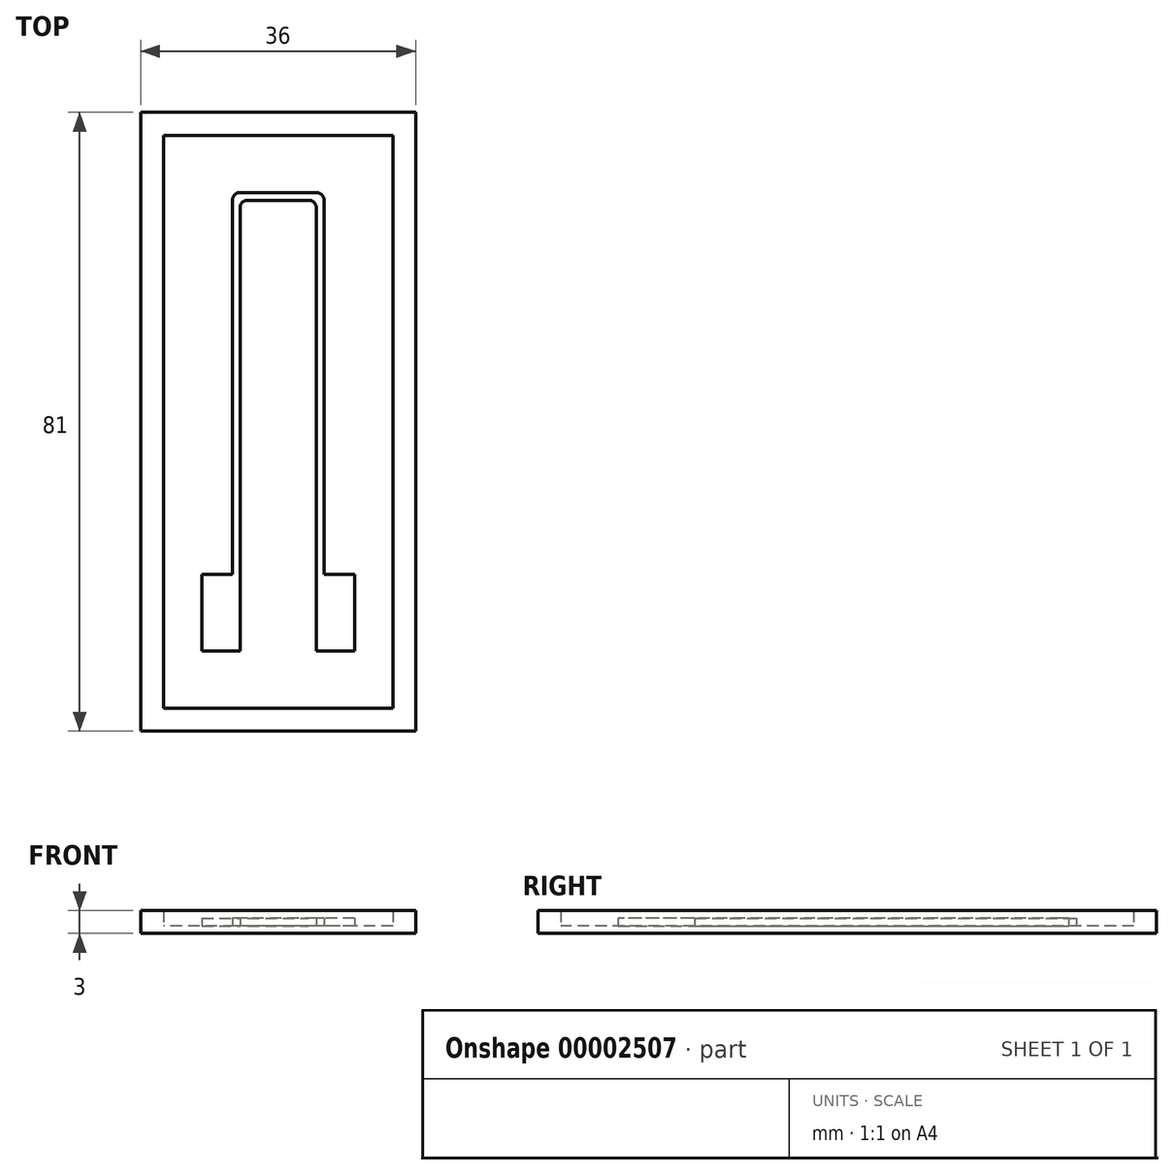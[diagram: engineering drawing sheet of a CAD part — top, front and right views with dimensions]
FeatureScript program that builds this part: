
annotation { "Feature Type Name" : "Feature", "Feature Type Description" : "" }
export const myFeature = defineFeature(function(context is Context, id is Id, definition is map)
    precondition{}
    {
        {
            var Q0;
            Q0=qCreatedBy(makeId("Top.planeOp"),FACE);
            var sketch = newSketch(context, id + "F0", { "sketchPlane" : qUnion([Q0])});
            skLineSegment(sketch, "E0.rect.bottom", {"start": v(15, 37.5) * mm, "end": v(-15, 37.5) * mm});
            skLineSegment(sketch, "E0.rect.top", {"start": v(15, -37.5) * mm, "end": v(-15, -37.5) * mm});
            skLineSegment(sketch, "E0.rect.left", {"start": v(15, 37.5) * mm, "end": v(15, -37.5) * mm});
            skLineSegment(sketch, "E0.rect.right", {"start": v(-15, 37.5) * mm, "end": v(-15, -37.5) * mm});
            skPoint(sketch, "E0.rect.middle", {"position": v(0, 0) * mm});
            skLineSegment(sketch, "E1", {"start": v(0, 0) * mm, "end": v(0, 17.9) * mm, "construction": true});
            skLineSegment(sketch, "E2.bottom", {"start": v(-10, -20) * mm, "end": v(-6, -20) * mm});
            skLineSegment(sketch, "E2.top", {"start": v(-10, -30) * mm, "end": v(-5, -30) * mm});
            skLineSegment(sketch, "E2.left", {"start": v(-10, -20) * mm, "end": v(-10, -30) * mm});
            skLineSegment(sketch, "E2.right", {"start": v(-5, -20) * mm, "end": v(-5, -30) * mm});
            skLineSegment(sketch, "E3", {"start": v(-5, -20) * mm, "end": v(-5, 28) * mm});
            skLineSegment(sketch, "E4", {"start": v(-4, 29) * mm, "end": v(0, 29) * mm});
            skLineSegment(sketch, "E5", {"start": v(-6, -20) * mm, "end": v(-6, 29) * mm});
            skLineSegment(sketch, "E6", {"start": v(-5, 30) * mm, "end": v(0, 30) * mm});
            skPoint(sketch, "E7.visualSharp", {"position": v(-6, 30) * mm});
            skArc(sketch, "E7.filletArc", {"start": v(-5, 30) * mm, "mid": v(-5.7, 29.7) * mm, "end": v(-6, 29) * mm});
            skArc(sketch, "E8.filletArc", {"start": v(-4, 29) * mm, "mid": v(-4.7, 28.7) * mm, "end": v(-5, 28) * mm});
            skLineSegment(sketch, "E9.0.MirrorCS", {"start": v(10, -30) * mm, "end": v(5, -30) * mm});
            skArc(sketch, "E9.1.MirrorCS", {"start": v(4, 29) * mm, "mid": v(4.7, 28.7) * mm, "end": v(5, 28) * mm});
            skArc(sketch, "E9.2.MirrorCS", {"start": v(5, 30) * mm, "mid": v(5.7, 29.7) * mm, "end": v(6, 29) * mm});
            skLineSegment(sketch, "E9.3.MirrorCS", {"start": v(10, -20) * mm, "end": v(6, -20) * mm});
            skLineSegment(sketch, "E9.4.MirrorCS", {"start": v(4, 29) * mm, "end": v(0, 29) * mm});
            skLineSegment(sketch, "E9.5.MirrorCS", {"start": v(5, 30) * mm, "end": v(0, 30) * mm});
            skPoint(sketch, "E9.6.MirrorP", {"position": v(6, 30) * mm});
            skLineSegment(sketch, "E9.8.MirrorCS", {"start": v(5, -20) * mm, "end": v(5, -30) * mm});
            skPoint(sketch, "E9.9.MirrorP", {"position": v(5, 29) * mm});
            skLineSegment(sketch, "E9.10.MirrorCS", {"start": v(6, -20) * mm, "end": v(6, 29) * mm});
            skLineSegment(sketch, "E9.11.MirrorCS", {"start": v(10, -20) * mm, "end": v(10, -30) * mm});
            skLineSegment(sketch, "E9.12.MirrorCS", {"start": v(5, -20) * mm, "end": v(5, 28) * mm});
            skLineSegment(sketch, "E10.0", {"start": v(18, 40.5) * mm, "end": v(-18, 40.5) * mm});
            skLineSegment(sketch, "E10.1", {"start": v(18, 40.5) * mm, "end": v(18, -40.5) * mm});
            skLineSegment(sketch, "E10.2", {"start": v(18, -40.5) * mm, "end": v(-18, -40.5) * mm});
            skLineSegment(sketch, "E10.3", {"start": v(-18, 40.5) * mm, "end": v(-18, -40.5) * mm});
            skSolve(sketch);
        }
        {
            var Q0;
            Q0=makeQuery(id+"F0.imprint","IMPRINT",FACE,{"disambiguationData":[TD([[makeQuery(id+"F0.imprint","IMPRINT",EDGE,{"derivedFrom":sQuery(id+"F0.wireOp",EDGE,"E0.rect.bottom")}),-1.0]])]});
            extrude(context, id + "F1", {"entities" : qUnion([Q0]), "depth" : 2 * mm});
        }
        {
            var Q0;
            Q0=makeQuery(id+"F0.imprint","IMPRINT",FACE,{"disambiguationData":[TD([[makeQuery(id+"F0.imprint","IMPRINT",EDGE,{"derivedFrom":sQuery(id+"F0.wireOp",EDGE,"E0.rect.bottom")}),1.0]])]});
            var Q1;
            Q1=makeQuery(id+"F1.opExtrude","CAP_FACE",FACE,{"disambiguationData":[OSD([sQuery(id+"F0.wireOp",EDGE,"E0.rect.bottom"),sQuery(id+"F0.wireOp",EDGE,"E0.rect.top"),sQuery(id+"F0.wireOp",EDGE,"E0.rect.left"),sQuery(id+"F0.wireOp",EDGE,"E0.rect.right"),sQuery(id+"F0.wireOp",EDGE,"E10.0"),sQuery(id+"F0.wireOp",EDGE,"E10.1"),sQuery(id+"F0.wireOp",EDGE,"E10.2"),sQuery(id+"F0.wireOp",EDGE,"E10.3")])],"isStart":false});
            var Q2;
            Q2=makeQuery(id+"F0.imprint","IMPRINT",FACE,{"disambiguationData":[TD([[makeQuery(id+"F0.imprint","IMPRINT",EDGE,{"derivedFrom":sQuery(id+"F0.wireOp",EDGE,"E2.bottom")}),-1.0]])]});
            extrude(context, id + "F2", {"entities" : qUnion([Q0, Q1, Q2]), "operationType" : NewBodyOperationType.ADD, "depth" : 1 * mm});
        }
        {
            var Q0;
            Q0=makeQuery(id+"F2.opExtrude","CAP_FACE",FACE,{"disambiguationData":[OSD([sQuery(id+"F0.wireOp",EDGE,"E0.rect.bottom"),sQuery(id+"F0.wireOp",EDGE,"E0.rect.top"),sQuery(id+"F0.wireOp",EDGE,"E0.rect.left"),sQuery(id+"F0.wireOp",EDGE,"E0.rect.right")])],"isStart":false});
            var sketch = newSketch(context, id + "F3", { "sketchPlane" : qUnion([Q0])});
            skLineSegment(sketch, "E11.0", {"start": v(-10, -20) * mm, "end": v(-10, -30) * mm});
            skLineSegment(sketch, "E12.0", {"start": v(-10, -30) * mm, "end": v(-5, -30) * mm});
            skLineSegment(sketch, "E13.0", {"start": v(-5, -20) * mm, "end": v(-5, -30) * mm});
            skLineSegment(sketch, "E14.0", {"start": v(-10, -20) * mm, "end": v(-6, -20) * mm});
            skLineSegment(sketch, "E15.0", {"start": v(-6, -20) * mm, "end": v(-6, 29) * mm});
            skLineSegment(sketch, "E16.0", {"start": v(-5, -20) * mm, "end": v(-5, 28) * mm});
            skArc(sketch, "E17.0", {"start": v(-5, 30) * mm, "mid": v(-5.7, 29.7) * mm, "end": v(-6, 29) * mm});
            skArc(sketch, "E18.0", {"start": v(-4, 29) * mm, "mid": v(-4.7, 28.7) * mm, "end": v(-5, 28) * mm});
            skLineSegment(sketch, "E19.0", {"start": v(-4, 29) * mm, "end": v(0, 29) * mm});
            skLineSegment(sketch, "E20.0", {"start": v(-5, 30) * mm, "end": v(0, 30) * mm});
            skLineSegment(sketch, "E21.0", {"start": v(4, 29) * mm, "end": v(0, 29) * mm});
            skLineSegment(sketch, "E22.0", {"start": v(5, 30) * mm, "end": v(0, 30) * mm});
            skArc(sketch, "E23.0", {"start": v(4, 29) * mm, "mid": v(4.7, 28.7) * mm, "end": v(5, 28) * mm});
            skArc(sketch, "E24.0", {"start": v(5, 30) * mm, "mid": v(5.7, 29.7) * mm, "end": v(6, 29) * mm});
            skLineSegment(sketch, "E25.0", {"start": v(5, -20) * mm, "end": v(5, 28) * mm});
            skLineSegment(sketch, "E26.0", {"start": v(6, -20) * mm, "end": v(6, 29) * mm});
            skLineSegment(sketch, "E27.0", {"start": v(5, -20) * mm, "end": v(5, -30) * mm});
            skLineSegment(sketch, "E28.0", {"start": v(10, -30) * mm, "end": v(5, -30) * mm});
            skLineSegment(sketch, "E29.0", {"start": v(10, -20) * mm, "end": v(10, -30) * mm});
            skLineSegment(sketch, "E30.0", {"start": v(10, -20) * mm, "end": v(6, -20) * mm});
            skSolve(sketch);
        }
        {
            var Q0;
            Q0=qSketchRegion(id+"F3",true);
            extrude(context, id + "F4", {"entities" : qUnion([Q0]), "operationType" : NewBodyOperationType.ADD, "depth" : 1 * mm});
        }
    });
